FCSTD DOCUMENT  (FreeCAD 0.18R4 (GitTag))
Label: pcb_0721
License: All rights reserved
LicenseURL: http://en.wikipedia.org/wiki/All_rights_reserved
objects: Part::Extrusion×98, Part::Feature×92, Part::Cut×38, Part::Part2DObjectPython×5, Part::MultiFuse×2
note: 235 computed .brp shape members not serialized (recipe doc carries the construction recipe); baked Part::Feature solids carry a one-line shape summary decoded from their .brp

FEATURE [Part::Feature] path847002
  shape: bbox 52.06 x 32.88 x 2e-07 mm, 1 faces, 0 solids (baked)
FEATURE [Part::Feature] path847003
  shape: bbox 1.07 x 1.07 x 2e-07 mm, 1 faces, 0 solids (baked)
FEATURE [Part::Feature] path847004
  shape: bbox 1.07 x 1.07 x 2e-07 mm, 1 faces, 0 solids (baked)
FEATURE [Part::Feature] path847005
  shape: bbox 1.07 x 1.07 x 2e-07 mm, 1 faces, 0 solids (baked)
FEATURE [Part::Feature] path847006
  shape: bbox 3.193 x 3.179 x 2e-07 mm, 1 faces, 0 solids (baked)
FEATURE [Part::Feature] path847007
  shape: bbox 2.86 x 2.857 x 2e-07 mm, 1 faces, 0 solids (baked)
FEATURE [Part::Feature] path847008
  shape: bbox 9.356 x 7.483 x 2e-07 mm, 1 faces, 0 solids (baked)
FEATURE [Part::Feature] path847009
  shape: bbox 0.8865 x 0.8873 x 2e-07 mm, 1 faces, 0 solids (baked)
FEATURE [Part::Feature] path847010
  shape: bbox 3.193 x 3.179 x 2e-07 mm, 1 faces, 0 solids (baked)
FEATURE [Part::Feature] path847011
  shape: bbox 2.86 x 2.857 x 2e-07 mm, 1 faces, 0 solids (baked)
FEATURE [Part::Feature] path847012
  shape: bbox 48.4 x 29.19 x 2e-07 mm, 1 faces, 0 solids (baked)
FEATURE [Part::Feature] path847013
  shape: bbox 0.8865 x 0.8873 x 2e-07 mm, 1 faces, 0 solids (baked)
FEATURE [Part::Feature] path847014
  shape: bbox 1.08 x 1.08 x 2e-07 mm, 1 faces, 0 solids (baked)
FEATURE [Part::Feature] path847015
  shape: bbox 1.051 x 1.08 x 2e-07 mm, 1 faces, 0 solids (baked)
FEATURE [Part::Feature] path847016
  shape: bbox 0.8865 x 0.8873 x 2e-07 mm, 1 faces, 0 solids (baked)
FEATURE [Part::Feature] path847017
  shape: bbox 1.051 x 1.08 x 2e-07 mm, 1 faces, 0 solids (baked)
FEATURE [Part::Feature] path847018
  shape: bbox 1.051 x 1.08 x 2e-07 mm, 1 faces, 0 solids (baked)
FEATURE [Part::Feature] path847019
  shape: bbox 0.8865 x 0.8873 x 2e-07 mm, 1 faces, 0 solids (baked)
FEATURE [Part::Feature] path847020
  shape: bbox 1.07 x 1.07 x 2e-07 mm, 1 faces, 0 solids (baked)
FEATURE [Part::Feature] path847021
  shape: bbox 1.07 x 1.07 x 2e-07 mm, 1 faces, 0 solids (baked)
FEATURE [Part::Feature] path847022
  shape: bbox 1.07 x 1.07 x 2e-07 mm, 1 faces, 0 solids (baked)
FEATURE [Part::Feature] path847023
  shape: bbox 5.68 x 13.71 x 2e-07 mm, 1 faces, 0 solids (baked)
FEATURE [Part::Feature] path847024
  shape: bbox 0.8865 x 0.8873 x 2e-07 mm, 1 faces, 0 solids (baked)
FEATURE [Part::Feature] path847025
  shape: bbox 2.945 x 12.44 x 2e-07 mm, 1 faces, 0 solids (baked)
FEATURE [Part::Feature] path847026
  shape: bbox 1.08 x 1.08 x 2e-07 mm, 1 faces, 0 solids (baked)
FEATURE [Part::Feature] path847027
  shape: bbox 3.892 x 11.64 x 2e-07 mm, 1 faces, 0 solids (baked)
FEATURE [Part::Feature] path847028
  shape: bbox 1.08 x 1.08 x 2e-07 mm, 1 faces, 0 solids (baked)
FEATURE [Part::Feature] path847029
  shape: bbox 3.945 x 10.51 x 2e-07 mm, 1 faces, 0 solids (baked)
FEATURE [Part::Feature] path847030
  shape: bbox 1.08 x 1.08 x 2e-07 mm, 1 faces, 0 solids (baked)
FEATURE [Part::Feature] path847031
  shape: bbox 7.44 x 14.82 x 2e-07 mm, 1 faces, 0 solids (baked)
FEATURE [Part::Feature] path847032
  shape: bbox 1.08 x 1.08 x 2e-07 mm, 1 faces, 0 solids (baked)
FEATURE [Part::Feature] path847033
  shape: bbox 6.314 x 15.06 x 2e-07 mm, 1 faces, 0 solids (baked)
FEATURE [Part::Feature] path847034
  shape: bbox 1.051 x 1.08 x 2e-07 mm, 1 faces, 0 solids (baked)
FEATURE [Part::Feature] path847035
  shape: bbox 1.051 x 1.08 x 2e-07 mm, 1 faces, 0 solids (baked)
FEATURE [Part::Feature] path847036
  shape: bbox 6.567 x 15.06 x 2e-07 mm, 1 faces, 0 solids (baked)
FEATURE [Part::Feature] path847037
  shape: bbox 1.051 x 1.08 x 2e-07 mm, 1 faces, 0 solids (baked)
FEATURE [Part::Feature] path847038
  shape: bbox 1.051 x 1.08 x 2e-07 mm, 1 faces, 0 solids (baked)
FEATURE [Part::Feature] path847039
  shape: bbox 1.051 x 1.08 x 2e-07 mm, 1 faces, 0 solids (baked)
FEATURE [Part::Feature] path847040
  shape: bbox 4.046 x 8.522 x 2e-07 mm, 1 faces, 0 solids (baked)
FEATURE [Part::Feature] path847041
  shape: bbox 1.051 x 1.08 x 2e-07 mm, 1 faces, 0 solids (baked)
FEATURE [Part::Feature] path847042
  shape: bbox 1.051 x 1.08 x 2e-07 mm, 1 faces, 0 solids (baked)
FEATURE [Part::Feature] path847043
  shape: bbox 6.997 x 11.98 x 2e-07 mm, 1 faces, 0 solids (baked)
FEATURE [Part::Feature] path847044
  shape: bbox 4.686 x 5.267 x 2e-07 mm, 1 faces, 0 solids (baked)
FEATURE [Part::Feature] path847045
  shape: bbox 3.177 x 19.4 x 2e-07 mm, 1 faces, 0 solids (baked)
FEATURE [Part::Feature] path847046
  shape: bbox 2.39 x 7.265 x 2e-07 mm, 1 faces, 0 solids (baked)
FEATURE [Part::Feature] path847047
  shape: bbox 3.317 x 3.796 x 2e-07 mm, 1 faces, 0 solids (baked)
FEATURE [Part::Feature] path847048
  shape: bbox 0.8865 x 0.8873 x 2e-07 mm, 1 faces, 0 solids (baked)
FEATURE [Part::Feature] path847049
  shape: bbox 1.509 x 4.212 x 2e-07 mm, 1 faces, 0 solids (baked)
FEATURE [Part::Feature] path847050
  shape: bbox 6.111 x 3.927 x 2e-07 mm, 1 faces, 0 solids (baked)
FEATURE [Part::Feature] path847051 .. path847054  x4 (patterned run collapsed; names and placements below)
  shape: bbox 0.5594 x 1.274 x 2e-07 mm, 1 faces, 0 solids (baked)
FEATURE [Part::Feature] path847055
  shape: bbox 1.277 x 0.5581 x 2e-07 mm, 1 faces, 0 solids (baked)
FEATURE [Part::Feature] path847056
  shape: bbox 1.277 x 0.5581 x 2e-07 mm, 1 faces, 0 solids (baked)
FEATURE [Part::Feature] path847057
  shape: bbox 2.818 x 3.254 x 2e-07 mm, 1 faces, 0 solids (baked)
FEATURE [Part::Feature] path847058
  shape: bbox 0.781 x 0.783 x 2e-07 mm, 1 faces, 0 solids (baked)
FEATURE [Part::Feature] path847059
  shape: bbox 2.206 x 0.6002 x 2e-07 mm, 1 faces, 0 solids (baked)
FEATURE [Part::Feature] path847060
  shape: bbox 1.277 x 0.5581 x 2e-07 mm, 1 faces, 0 solids (baked)
FEATURE [Part::Feature] path847061
  shape: bbox 1.277 x 0.5581 x 2e-07 mm, 1 faces, 0 solids (baked)
FEATURE [Part::Feature] path847062
  shape: bbox 1.277 x 0.5581 x 2e-07 mm, 1 faces, 0 solids (baked)
FEATURE [Part::Feature] path847063
  shape: bbox 3.367 x 1.611 x 2e-07 mm, 1 faces, 0 solids (baked)
FEATURE [Part::Feature] path847064
  shape: bbox 0.781 x 0.783 x 2e-07 mm, 1 faces, 0 solids (baked)
FEATURE [Part::Feature] path847065
  shape: bbox 9.762 x 5.519 x 2e-07 mm, 1 faces, 0 solids (baked)
FEATURE [Part::Feature] path847066
  shape: bbox 2.206 x 0.6002 x 2e-07 mm, 1 faces, 0 solids (baked)
FEATURE [Part::Feature] path847067
  shape: bbox 2.206 x 0.6002 x 2e-07 mm, 1 faces, 0 solids (baked)
FEATURE [Part::Feature] path847068
  shape: bbox 5.456 x 11.92 x 2e-07 mm, 1 faces, 0 solids (baked)
FEATURE [Part::Feature] path847069
  shape: bbox 0.781 x 0.783 x 2e-07 mm, 1 faces, 0 solids (baked)
FEATURE [Part::Feature] path847070
  shape: bbox 0.8865 x 0.8873 x 2e-07 mm, 1 faces, 0 solids (baked)
FEATURE [Part::Feature] path847071
  shape: bbox 4.58 x 1.611 x 2e-07 mm, 1 faces, 0 solids (baked)
FEATURE [Part::Feature] path847072
  shape: bbox 0.781 x 0.783 x 2e-07 mm, 1 faces, 0 solids (baked)
FEATURE [Part::Feature] path847073
  shape: bbox 1.277 x 0.5581 x 2e-07 mm, 1 faces, 0 solids (baked)
FEATURE [Part::Feature] path847074
  shape: bbox 18.21 x 6.191 x 2e-07 mm, 1 faces, 0 solids (baked)
FEATURE [Part::Feature] path847075
  shape: bbox 12.52 x 5.875 x 2e-07 mm, 1 faces, 0 solids (baked)
FEATURE [Part::Feature] path847076
  shape: bbox 3.887 x 4.512 x 2e-07 mm, 1 faces, 0 solids (baked)
FEATURE [Part::Feature] path847077
  shape: bbox 0.781 x 0.783 x 2e-07 mm, 1 faces, 0 solids (baked)
FEATURE [Part::Feature] path847078
  shape: bbox 0.8865 x 0.8873 x 2e-07 mm, 1 faces, 0 solids (baked)
FEATURE [Part::Feature] path847079
  shape: bbox 3.261 x 1.611 x 2e-07 mm, 1 faces, 0 solids (baked)
FEATURE [Part::Feature] path847080
  shape: bbox 0.781 x 0.783 x 2e-07 mm, 1 faces, 0 solids (baked)
FEATURE [Part::Feature] path847081
  shape: bbox 15.05 x 6.086 x 2e-07 mm, 1 faces, 0 solids (baked)
FEATURE [Part::Feature] path847082
  shape: bbox 9.667 x 8.824 x 2e-07 mm, 1 faces, 0 solids (baked)
FEATURE [Part::Feature] path847083
  shape: bbox 7.852 x 8.824 x 2e-07 mm, 1 faces, 0 solids (baked)
FEATURE [Part::Feature] path847084
  shape: bbox 0.5594 x 1.274 x 2e-07 mm, 1 faces, 0 solids (baked)
FEATURE [Part::Feature] path847085
  shape: bbox 0.5594 x 1.274 x 2e-07 mm, 1 faces, 0 solids (baked)
FEATURE [Part::Feature] path847086
  shape: bbox 7.129 x 2.592 x 2e-07 mm, 1 faces, 0 solids (baked)
FEATURE [Part::Feature] path847087
  shape: bbox 0.8865 x 0.8873 x 2e-07 mm, 1 faces, 0 solids (baked)
FEATURE [Part::Feature] path847088
  shape: bbox 7.129 x 3.676 x 2e-07 mm, 1 faces, 0 solids (baked)
FEATURE [Part::Feature] path847089
  shape: bbox 0.8865 x 0.8873 x 2e-07 mm, 1 faces, 0 solids (baked)
FEATURE [Part::Feature] path847090
  shape: bbox 3.193 x 3.187 x 2e-07 mm, 1 faces, 0 solids (baked)
FEATURE [Part::Feature] path847091
  shape: bbox 2.86 x 2.857 x 2e-07 mm, 1 faces, 0 solids (baked)
FEATURE [Part::Feature] path847092
  shape: bbox 3.193 x 3.187 x 2e-07 mm, 1 faces, 0 solids (baked)
FEATURE [Part::Feature] path847093
  shape: bbox 2.86 x 2.857 x 2e-07 mm, 1 faces, 0 solids (baked)
FEATURE [Part::Extrusion] Extrude
  Base = -> path847002
  Dir = (0,0,1)
  DirMode = 0
  FaceMakerClass = Part::FaceMakerBullseye
  LengthFwd = 10
  LengthRev = 0
  Solid = false
  Symmetric = false
FEATURE [Part::Extrusion] Extrude001
  Base = -> path847003
  Dir = (0,0,1)
  DirMode = 0
  FaceMakerClass = Part::FaceMakerBullseye
  LengthFwd = 10
  LengthRev = 0
  Solid = false
  Symmetric = false
FEATURE [Part::Extrusion] Extrude002
  Base = -> path847004
  Dir = (0,0,1)
  DirMode = 0
  FaceMakerClass = Part::FaceMakerBullseye
  LengthFwd = 10
  LengthRev = 0
  Solid = false
  Symmetric = false
FEATURE [Part::Extrusion] Extrude003
  Base = -> path847005
  Dir = (0,0,1)
  DirMode = 0
  FaceMakerClass = Part::FaceMakerBullseye
  LengthFwd = 10
  LengthRev = 0
  Solid = false
  Symmetric = false
FEATURE [Part::Extrusion] Extrude004
  Base = -> path847006
  Dir = (0,0,1)
  DirMode = 0
  FaceMakerClass = Part::FaceMakerBullseye
  LengthFwd = 10
  LengthRev = 0
  Solid = false
  Symmetric = false
FEATURE [Part::Extrusion] Extrude005
  Base = -> path847007
  Dir = (0,0,1)
  DirMode = 0
  FaceMakerClass = Part::FaceMakerBullseye
  LengthFwd = 10
  LengthRev = 0
  Solid = false
  Symmetric = false
FEATURE [Part::Extrusion] Extrude006
  Base = -> path847008
  Dir = (0,0,1)
  DirMode = 0
  FaceMakerClass = Part::FaceMakerBullseye
  LengthFwd = 10
  LengthRev = 0
  Solid = false
  Symmetric = false
FEATURE [Part::Extrusion] Extrude007
  Base = -> path847009
  Dir = (0,0,1)
  DirMode = 0
  FaceMakerClass = Part::FaceMakerBullseye
  LengthFwd = 10
  LengthRev = 0
  Solid = false
  Symmetric = false
FEATURE [Part::Extrusion] Extrude008
  Base = -> path847010
  Dir = (0,0,1)
  DirMode = 0
  FaceMakerClass = Part::FaceMakerBullseye
  LengthFwd = 10
  LengthRev = 0
  Solid = false
  Symmetric = false
FEATURE [Part::Extrusion] Extrude009
  Base = -> path847011
  Dir = (0,0,1)
  DirMode = 0
  FaceMakerClass = Part::FaceMakerBullseye
  LengthFwd = 10
  LengthRev = 0
  Solid = false
  Symmetric = false
FEATURE [Part::Extrusion] Extrude010
  Base = -> path847012
  Dir = (0,0,1)
  DirMode = 0
  FaceMakerClass = Part::FaceMakerBullseye
  LengthFwd = 10
  LengthRev = 0
  Solid = false
  Symmetric = false
FEATURE [Part::Extrusion] Extrude011
  Base = -> path847013
  Dir = (0,0,1)
  DirMode = 0
  FaceMakerClass = Part::FaceMakerBullseye
  LengthFwd = 10
  LengthRev = 0
  Solid = false
  Symmetric = false
FEATURE [Part::Extrusion] Extrude012
  Base = -> path847014
  Dir = (0,0,1)
  DirMode = 0
  FaceMakerClass = Part::FaceMakerBullseye
  LengthFwd = 10
  LengthRev = 0
  Solid = false
  Symmetric = false
FEATURE [Part::Extrusion] Extrude013
  Base = -> path847015
  Dir = (0,0,1)
  DirMode = 0
  FaceMakerClass = Part::FaceMakerBullseye
  LengthFwd = 10
  LengthRev = 0
  Solid = false
  Symmetric = false
FEATURE [Part::Extrusion] Extrude014
  Base = -> path847016
  Dir = (0,0,1)
  DirMode = 0
  FaceMakerClass = Part::FaceMakerBullseye
  LengthFwd = 10
  LengthRev = 0
  Solid = false
  Symmetric = false
FEATURE [Part::Extrusion] Extrude015
  Base = -> path847017
  Dir = (0,0,1)
  DirMode = 0
  FaceMakerClass = Part::FaceMakerBullseye
  LengthFwd = 10
  LengthRev = 0
  Solid = false
  Symmetric = false
FEATURE [Part::Extrusion] Extrude016
  Base = -> path847018
  Dir = (0,0,1)
  DirMode = 0
  FaceMakerClass = Part::FaceMakerBullseye
  LengthFwd = 10
  LengthRev = 0
  Solid = false
  Symmetric = false
FEATURE [Part::Extrusion] Extrude017
  Base = -> path847019
  Dir = (0,0,1)
  DirMode = 0
  FaceMakerClass = Part::FaceMakerBullseye
  LengthFwd = 10
  LengthRev = 0
  Solid = false
  Symmetric = false
FEATURE [Part::Extrusion] Extrude018
  Base = -> path847020
  Dir = (0,0,1)
  DirMode = 0
  FaceMakerClass = Part::FaceMakerBullseye
  LengthFwd = 10
  LengthRev = 0
  Solid = false
  Symmetric = false
FEATURE [Part::Extrusion] Extrude019
  Base = -> path847021
  Dir = (0,0,1)
  DirMode = 0
  FaceMakerClass = Part::FaceMakerBullseye
  LengthFwd = 10
  LengthRev = 0
  Solid = false
  Symmetric = false
FEATURE [Part::Extrusion] Extrude020
  Base = -> path847022
  Dir = (0,0,1)
  DirMode = 0
  FaceMakerClass = Part::FaceMakerBullseye
  LengthFwd = 10
  LengthRev = 0
  Solid = false
  Symmetric = false
FEATURE [Part::Extrusion] Extrude021
  Base = -> path847023
  Dir = (0,0,1)
  DirMode = 0
  FaceMakerClass = Part::FaceMakerBullseye
  LengthFwd = 10
  LengthRev = 0
  Solid = false
  Symmetric = false
FEATURE [Part::Extrusion] Extrude022
  Base = -> path847024
  Dir = (0,0,1)
  DirMode = 0
  FaceMakerClass = Part::FaceMakerBullseye
  LengthFwd = 10
  LengthRev = 0
  Solid = false
  Symmetric = false
FEATURE [Part::Extrusion] Extrude023
  Base = -> path847025
  Dir = (0,0,1)
  DirMode = 0
  FaceMakerClass = Part::FaceMakerBullseye
  LengthFwd = 10
  LengthRev = 0
  Solid = false
  Symmetric = false
FEATURE [Part::Extrusion] Extrude024
  Base = -> path847026
  Dir = (0,0,1)
  DirMode = 0
  FaceMakerClass = Part::FaceMakerBullseye
  LengthFwd = 10
  LengthRev = 0
  Solid = false
  Symmetric = false
FEATURE [Part::Extrusion] Extrude025
  Base = -> path847027
  Dir = (0,0,1)
  DirMode = 0
  FaceMakerClass = Part::FaceMakerBullseye
  LengthFwd = 10
  LengthRev = 0
  Solid = false
  Symmetric = false
FEATURE [Part::Extrusion] Extrude026
  Base = -> path847028
  Dir = (0,0,1)
  DirMode = 0
  FaceMakerClass = Part::FaceMakerBullseye
  LengthFwd = 10
  LengthRev = 0
  Solid = false
  Symmetric = false
FEATURE [Part::Extrusion] Extrude027
  Base = -> path847029
  Dir = (0,0,1)
  DirMode = 0
  FaceMakerClass = Part::FaceMakerBullseye
  LengthFwd = 10
  LengthRev = 0
  Solid = false
  Symmetric = false
FEATURE [Part::Extrusion] Extrude028
  Base = -> path847030
  Dir = (0,0,1)
  DirMode = 0
  FaceMakerClass = Part::FaceMakerBullseye
  LengthFwd = 10
  LengthRev = 0
  Solid = false
  Symmetric = false
FEATURE [Part::Extrusion] Extrude029
  Base = -> path847031
  Dir = (0,0,1)
  DirMode = 0
  FaceMakerClass = Part::FaceMakerBullseye
  LengthFwd = 10
  LengthRev = 0
  Solid = false
  Symmetric = false
FEATURE [Part::Extrusion] Extrude030
  Base = -> path847032
  Dir = (0,0,1)
  DirMode = 0
  FaceMakerClass = Part::FaceMakerBullseye
  LengthFwd = 10
  LengthRev = 0
  Solid = false
  Symmetric = false
FEATURE [Part::Extrusion] Extrude031
  Base = -> path847033
  Dir = (0,0,1)
  DirMode = 0
  FaceMakerClass = Part::FaceMakerBullseye
  LengthFwd = 10
  LengthRev = 0
  Solid = false
  Symmetric = false
FEATURE [Part::Extrusion] Extrude032
  Base = -> path847034
  Dir = (0,0,1)
  DirMode = 0
  FaceMakerClass = Part::FaceMakerBullseye
  LengthFwd = 10
  LengthRev = 0
  Solid = false
  Symmetric = false
FEATURE [Part::Extrusion] Extrude033
  Base = -> path847035
  Dir = (0,0,1)
  DirMode = 0
  FaceMakerClass = Part::FaceMakerBullseye
  LengthFwd = 10
  LengthRev = 0
  Solid = false
  Symmetric = false
FEATURE [Part::Extrusion] Extrude034
  Base = -> path847036
  Dir = (0,0,1)
  DirMode = 0
  FaceMakerClass = Part::FaceMakerBullseye
  LengthFwd = 10
  LengthRev = 0
  Solid = false
  Symmetric = false
FEATURE [Part::Extrusion] Extrude035
  Base = -> path847037
  Dir = (0,0,1)
  DirMode = 0
  FaceMakerClass = Part::FaceMakerBullseye
  LengthFwd = 10
  LengthRev = 0
  Solid = false
  Symmetric = false
FEATURE [Part::Extrusion] Extrude036
  Base = -> path847038
  Dir = (0,0,1)
  DirMode = 0
  FaceMakerClass = Part::FaceMakerBullseye
  LengthFwd = 10
  LengthRev = 0
  Solid = false
  Symmetric = false
FEATURE [Part::Extrusion] Extrude037
  Base = -> path847039
  Dir = (0,0,1)
  DirMode = 0
  FaceMakerClass = Part::FaceMakerBullseye
  LengthFwd = 10
  LengthRev = 0
  Solid = false
  Symmetric = false
FEATURE [Part::Extrusion] Extrude038
  Base = -> path847040
  Dir = (0,0,1)
  DirMode = 0
  FaceMakerClass = Part::FaceMakerBullseye
  LengthFwd = 10
  LengthRev = 0
  Solid = false
  Symmetric = false
FEATURE [Part::Extrusion] Extrude039
  Base = -> path847041
  Dir = (0,0,1)
  DirMode = 0
  FaceMakerClass = Part::FaceMakerBullseye
  LengthFwd = 10
  LengthRev = 0
  Solid = false
  Symmetric = false
FEATURE [Part::Extrusion] Extrude040
  Base = -> path847042
  Dir = (0,0,1)
  DirMode = 0
  FaceMakerClass = Part::FaceMakerBullseye
  LengthFwd = 10
  LengthRev = 0
  Solid = false
  Symmetric = false
FEATURE [Part::Extrusion] Extrude041
  Base = -> path847043
  Dir = (0,0,1)
  DirMode = 0
  FaceMakerClass = Part::FaceMakerBullseye
  LengthFwd = 10
  LengthRev = 0
  Solid = false
  Symmetric = false
FEATURE [Part::Extrusion] Extrude042
  Base = -> path847044
  Dir = (0,0,1)
  DirMode = 0
  FaceMakerClass = Part::FaceMakerBullseye
  LengthFwd = 10
  LengthRev = 0
  Solid = false
  Symmetric = false
FEATURE [Part::Extrusion] Extrude043
  Base = -> path847045
  Dir = (0,0,1)
  DirMode = 0
  FaceMakerClass = Part::FaceMakerBullseye
  LengthFwd = 10
  LengthRev = 0
  Solid = false
  Symmetric = false
FEATURE [Part::Extrusion] Extrude044
  Base = -> path847046
  Dir = (0,0,1)
  DirMode = 0
  FaceMakerClass = Part::FaceMakerBullseye
  LengthFwd = 10
  LengthRev = 0
  Solid = false
  Symmetric = false
FEATURE [Part::Extrusion] Extrude045
  Base = -> path847047
  Dir = (0,0,1)
  DirMode = 0
  FaceMakerClass = Part::FaceMakerBullseye
  LengthFwd = 10
  LengthRev = 0
  Solid = false
  Symmetric = false
FEATURE [Part::Extrusion] Extrude046
  Base = -> path847048
  Dir = (0,0,1)
  DirMode = 0
  FaceMakerClass = Part::FaceMakerBullseye
  LengthFwd = 10
  LengthRev = 0
  Solid = false
  Symmetric = false
FEATURE [Part::Extrusion] Extrude047
  Base = -> path847049
  Dir = (0,0,1)
  DirMode = 0
  FaceMakerClass = Part::FaceMakerBullseye
  LengthFwd = 10
  LengthRev = 0
  Solid = false
  Symmetric = false
FEATURE [Part::Extrusion] Extrude048
  Base = -> path847050
  Dir = (0,0,1)
  DirMode = 0
  FaceMakerClass = Part::FaceMakerBullseye
  LengthFwd = 10
  LengthRev = 0
  Solid = false
  Symmetric = false
FEATURE [Part::Extrusion] Extrude049
  Base = -> path847051
  Dir = (0,0,1)
  DirMode = 0
  FaceMakerClass = Part::FaceMakerBullseye
  LengthFwd = 10
  LengthRev = 0
  Solid = false
  Symmetric = false
FEATURE [Part::Extrusion] Extrude050
  Base = -> path847052
  Dir = (0,0,1)
  DirMode = 0
  FaceMakerClass = Part::FaceMakerBullseye
  LengthFwd = 10
  LengthRev = 0
  Solid = false
  Symmetric = false
FEATURE [Part::Extrusion] Extrude051
  Base = -> path847053
  Dir = (0,0,1)
  DirMode = 0
  FaceMakerClass = Part::FaceMakerBullseye
  LengthFwd = 10
  LengthRev = 0
  Solid = false
  Symmetric = false
FEATURE [Part::Extrusion] Extrude052
  Base = -> path847054
  Dir = (0,0,1)
  DirMode = 0
  FaceMakerClass = Part::FaceMakerBullseye
  LengthFwd = 10
  LengthRev = 0
  Solid = false
  Symmetric = false
FEATURE [Part::Extrusion] Extrude053
  Base = -> path847055
  Dir = (0,0,1)
  DirMode = 0
  FaceMakerClass = Part::FaceMakerBullseye
  LengthFwd = 10
  LengthRev = 0
  Solid = false
  Symmetric = false
FEATURE [Part::Extrusion] Extrude054
  Base = -> path847056
  Dir = (0,0,1)
  DirMode = 0
  FaceMakerClass = Part::FaceMakerBullseye
  LengthFwd = 10
  LengthRev = 0
  Solid = false
  Symmetric = false
FEATURE [Part::Extrusion] Extrude055
  Base = -> path847057
  Dir = (0,0,1)
  DirMode = 0
  FaceMakerClass = Part::FaceMakerBullseye
  LengthFwd = 10
  LengthRev = 0
  Solid = false
  Symmetric = false
FEATURE [Part::Extrusion] Extrude056
  Base = -> path847058
  Dir = (0,0,1)
  DirMode = 0
  FaceMakerClass = Part::FaceMakerBullseye
  LengthFwd = 10
  LengthRev = 0
  Solid = false
  Symmetric = false
FEATURE [Part::Extrusion] Extrude057
  Base = -> path847059
  Dir = (0,0,1)
  DirMode = 0
  FaceMakerClass = Part::FaceMakerBullseye
  LengthFwd = 10
  LengthRev = 0
  Solid = false
  Symmetric = false
FEATURE [Part::Extrusion] Extrude058
  Base = -> path847060
  Dir = (0,0,1)
  DirMode = 0
  FaceMakerClass = Part::FaceMakerBullseye
  LengthFwd = 10
  LengthRev = 0
  Solid = false
  Symmetric = false
FEATURE [Part::Extrusion] Extrude059
  Base = -> path847061
  Dir = (0,0,1)
  DirMode = 0
  FaceMakerClass = Part::FaceMakerBullseye
  LengthFwd = 10
  LengthRev = 0
  Solid = false
  Symmetric = false
FEATURE [Part::Extrusion] Extrude060
  Base = -> path847062
  Dir = (0,0,1)
  DirMode = 0
  FaceMakerClass = Part::FaceMakerBullseye
  LengthFwd = 10
  LengthRev = 0
  Solid = false
  Symmetric = false
FEATURE [Part::Extrusion] Extrude061
  Base = -> path847063
  Dir = (0,0,1)
  DirMode = 0
  FaceMakerClass = Part::FaceMakerBullseye
  LengthFwd = 10
  LengthRev = 0
  Solid = false
  Symmetric = false
FEATURE [Part::Extrusion] Extrude062
  Base = -> path847064
  Dir = (0,0,1)
  DirMode = 0
  FaceMakerClass = Part::FaceMakerBullseye
  LengthFwd = 10
  LengthRev = 0
  Solid = false
  Symmetric = false
FEATURE [Part::Extrusion] Extrude063
  Base = -> path847065
  Dir = (0,0,1)
  DirMode = 0
  FaceMakerClass = Part::FaceMakerBullseye
  LengthFwd = 10
  LengthRev = 0
  Solid = false
  Symmetric = false
FEATURE [Part::Extrusion] Extrude064
  Base = -> path847066
  Dir = (0,0,1)
  DirMode = 0
  FaceMakerClass = Part::FaceMakerBullseye
  LengthFwd = 10
  LengthRev = 0
  Solid = false
  Symmetric = false
FEATURE [Part::Extrusion] Extrude065
  Base = -> path847067
  Dir = (0,0,1)
  DirMode = 0
  FaceMakerClass = Part::FaceMakerBullseye
  LengthFwd = 10
  LengthRev = 0
  Solid = false
  Symmetric = false
FEATURE [Part::Extrusion] Extrude066
  Base = -> path847068
  Dir = (0,0,1)
  DirMode = 0
  FaceMakerClass = Part::FaceMakerBullseye
  LengthFwd = 10
  LengthRev = 0
  Solid = false
  Symmetric = false
FEATURE [Part::Extrusion] Extrude067
  Base = -> path847069
  Dir = (0,0,1)
  DirMode = 0
  FaceMakerClass = Part::FaceMakerBullseye
  LengthFwd = 10
  LengthRev = 0
  Solid = false
  Symmetric = false
FEATURE [Part::Extrusion] Extrude068
  Base = -> path847070
  Dir = (0,0,1)
  DirMode = 0
  FaceMakerClass = Part::FaceMakerBullseye
  LengthFwd = 10
  LengthRev = 0
  Solid = false
  Symmetric = false
FEATURE [Part::Extrusion] Extrude069
  Base = -> path847071
  Dir = (0,0,1)
  DirMode = 0
  FaceMakerClass = Part::FaceMakerBullseye
  LengthFwd = 10
  LengthRev = 0
  Solid = false
  Symmetric = false
FEATURE [Part::Extrusion] Extrude070
  Base = -> path847072
  Dir = (0,0,1)
  DirMode = 0
  FaceMakerClass = Part::FaceMakerBullseye
  LengthFwd = 10
  LengthRev = 0
  Solid = false
  Symmetric = false
FEATURE [Part::Extrusion] Extrude071
  Base = -> path847073
  Dir = (0,0,1)
  DirMode = 0
  FaceMakerClass = Part::FaceMakerBullseye
  LengthFwd = 10
  LengthRev = 0
  Solid = false
  Symmetric = false
FEATURE [Part::Extrusion] Extrude072
  Base = -> path847074
  Dir = (0,0,1)
  DirMode = 0
  FaceMakerClass = Part::FaceMakerBullseye
  LengthFwd = 10
  LengthRev = 0
  Solid = false
  Symmetric = false
FEATURE [Part::Extrusion] Extrude073
  Base = -> path847075
  Dir = (0,0,1)
  DirMode = 0
  FaceMakerClass = Part::FaceMakerBullseye
  LengthFwd = 10
  LengthRev = 0
  Solid = false
  Symmetric = false
FEATURE [Part::Extrusion] Extrude074
  Base = -> path847076
  Dir = (0,0,1)
  DirMode = 0
  FaceMakerClass = Part::FaceMakerBullseye
  LengthFwd = 10
  LengthRev = 0
  Solid = false
  Symmetric = false
FEATURE [Part::Extrusion] Extrude075
  Base = -> path847077
  Dir = (0,0,1)
  DirMode = 0
  FaceMakerClass = Part::FaceMakerBullseye
  LengthFwd = 10
  LengthRev = 0
  Solid = false
  Symmetric = false
FEATURE [Part::Extrusion] Extrude076
  Base = -> path847078
  Dir = (0,0,1)
  DirMode = 0
  FaceMakerClass = Part::FaceMakerBullseye
  LengthFwd = 10
  LengthRev = 0
  Solid = false
  Symmetric = false
FEATURE [Part::Extrusion] Extrude077
  Base = -> path847079
  Dir = (0,0,1)
  DirMode = 0
  FaceMakerClass = Part::FaceMakerBullseye
  LengthFwd = 10
  LengthRev = 0
  Solid = false
  Symmetric = false
FEATURE [Part::Extrusion] Extrude078
  Base = -> path847080
  Dir = (0,0,1)
  DirMode = 0
  FaceMakerClass = Part::FaceMakerBullseye
  LengthFwd = 10
  LengthRev = 0
  Solid = false
  Symmetric = false
FEATURE [Part::Extrusion] Extrude079
  Base = -> path847081
  Dir = (0,0,1)
  DirMode = 0
  FaceMakerClass = Part::FaceMakerBullseye
  LengthFwd = 10
  LengthRev = 0
  Solid = false
  Symmetric = false
FEATURE [Part::Extrusion] Extrude080
  Base = -> path847082
  Dir = (0,0,1)
  DirMode = 0
  FaceMakerClass = Part::FaceMakerBullseye
  LengthFwd = 10
  LengthRev = 0
  Solid = false
  Symmetric = false
FEATURE [Part::Extrusion] Extrude081
  Base = -> path847083
  Dir = (0,0,1)
  DirMode = 0
  FaceMakerClass = Part::FaceMakerBullseye
  LengthFwd = 10
  LengthRev = 0
  Solid = false
  Symmetric = false
FEATURE [Part::Extrusion] Extrude082
  Base = -> path847084
  Dir = (0,0,1)
  DirMode = 0
  FaceMakerClass = Part::FaceMakerBullseye
  LengthFwd = 10
  LengthRev = 0
  Solid = false
  Symmetric = false
FEATURE [Part::Extrusion] Extrude083
  Base = -> path847085
  Dir = (0,0,1)
  DirMode = 0
  FaceMakerClass = Part::FaceMakerBullseye
  LengthFwd = 10
  LengthRev = 0
  Solid = false
  Symmetric = false
FEATURE [Part::Extrusion] Extrude084
  Base = -> path847086
  Dir = (0,0,1)
  DirMode = 0
  FaceMakerClass = Part::FaceMakerBullseye
  LengthFwd = 10
  LengthRev = 0
  Solid = false
  Symmetric = false
FEATURE [Part::Extrusion] Extrude085
  Base = -> path847087
  Dir = (0,0,1)
  DirMode = 0
  FaceMakerClass = Part::FaceMakerBullseye
  LengthFwd = 10
  LengthRev = 0
  Solid = false
  Symmetric = false
FEATURE [Part::Extrusion] Extrude086
  Base = -> path847088
  Dir = (0,0,1)
  DirMode = 0
  FaceMakerClass = Part::FaceMakerBullseye
  LengthFwd = 10
  LengthRev = 0
  Solid = false
  Symmetric = false
FEATURE [Part::Extrusion] Extrude087
  Base = -> path847089
  Dir = (0,0,1)
  DirMode = 0
  FaceMakerClass = Part::FaceMakerBullseye
  LengthFwd = 10
  LengthRev = 0
  Solid = false
  Symmetric = false
FEATURE [Part::Extrusion] Extrude088
  Base = -> path847090
  Dir = (0,0,1)
  DirMode = 0
  FaceMakerClass = Part::FaceMakerBullseye
  LengthFwd = 10
  LengthRev = 0
  Solid = false
  Symmetric = false
FEATURE [Part::Extrusion] Extrude089
  Base = -> path847091
  Dir = (0,0,1)
  DirMode = 0
  FaceMakerClass = Part::FaceMakerBullseye
  LengthFwd = 10
  LengthRev = 0
  Solid = false
  Symmetric = false
FEATURE [Part::Extrusion] Extrude090
  Base = -> path847092
  Dir = (0,0,1)
  DirMode = 0
  FaceMakerClass = Part::FaceMakerBullseye
  LengthFwd = 10
  LengthRev = 0
  Solid = false
  Symmetric = false
FEATURE [Part::Extrusion] Extrude091
  Base = -> path847093
  Dir = (0,0,1)
  DirMode = 0
  FaceMakerClass = Part::FaceMakerBullseye
  LengthFwd = 10
  LengthRev = 0
  Solid = false
  Symmetric = false
FEATURE [Part::Cut] Cut
  Base = -> Extrude061
  Tool = -> Extrude062
FEATURE [Part::Cut] Cut001
  Base = -> Extrude069
  Tool = -> Extrude070
FEATURE [Part::Cut] Cut002
  Base = -> Extrude077
  Tool = -> Extrude078
FEATURE [Part::Cut] Cut003
  Base = -> Extrude074
  Tool = -> Extrude076
FEATURE [Part::Cut] Cut004
  Base = -> Cut003
  Tool = -> Extrude075
FEATURE [Part::Cut] Cut005
  Base = -> Extrude084
  Tool = -> Extrude085
FEATURE [Part::Cut] Cut006
  Base = -> Extrude066
  Tool = -> Extrude067
FEATURE [Part::Cut] Cut007
  Base = -> Extrude055
  Tool = -> Extrude056
FEATURE [Part::Cut] Cut008
  Base = -> Cut006
  Tool = -> Extrude068
FEATURE [Part::Cut] Cut009
  Base = -> Extrude086
  Tool = -> Extrude087
FEATURE [Part::Cut] Cut010
  Base = -> Extrude045
  Tool = -> Extrude046
FEATURE [Part::Cut] Cut011
  Base = -> Extrude010
  Tool = -> Extrude017
FEATURE [Part::Cut] Cut012
  Base = -> Cut011
  Tool = -> Extrude014
FEATURE [Part::Cut] Cut013
  Base = -> Cut012
  Tool = -> Extrude011
FEATURE [Part::Cut] Cut014
  Base = -> Extrude006
  Tool = -> Extrude007
FEATURE [Part::Cut] Cut015
  Base = -> Cut013
  Tool = -> Extrude018
FEATURE [Part::Cut] Cut016
  Base = -> Cut015
  Tool = -> Extrude019
FEATURE [Part::Cut] Cut017
  Base = -> Cut016
  Tool = -> Extrude020
FEATURE [Part::Cut] Cut018
  Base = -> Extrude
  Tool = -> Extrude001
FEATURE [Part::Cut] Cut019
  Base = -> Cut018
  Tool = -> Extrude002
FEATURE [Part::Cut] Cut020
  Base = -> Cut019
  Tool = -> Extrude003
FEATURE [Part::Cut] Cut021
  Base = -> Extrude023
  Tool = -> Extrude024
FEATURE [Part::Cut] Cut022
  Base = -> Extrude025
  Tool = -> Extrude026
FEATURE [Part::Cut] Cut023
  Base = -> Extrude027
  Tool = -> Extrude028
FEATURE [Part::Cut] Cut024
  Base = -> Cut017
  Tool = -> Extrude012
FEATURE [Part::Cut] Cut025
  Base = -> Extrude029
  Tool = -> Extrude030
FEATURE [Part::Cut] Cut026
  Base = -> Cut024
  Tool = -> Extrude015
FEATURE [Part::Cut] Cut027
  Base = -> Cut026
  Tool = -> Extrude016
FEATURE [Part::Cut] Cut028
  Base = -> Cut027
  Tool = -> Extrude013
FEATURE [Part::Cut] Cut029
  Base = -> Extrude034
  Tool = -> Extrude035
FEATURE [Part::Cut] Cut030
  Base = -> Cut029
  Tool = -> Extrude036
FEATURE [Part::Cut] Cut031
  Base = -> Cut030
  Tool = -> Extrude037
FEATURE [Part::Cut] Cut032
  Base = -> Extrude038
  Tool = -> Extrude040
FEATURE [Part::Cut] Cut033
  Base = -> Cut032
  Tool = -> Extrude039
FEATURE [Part::Cut] Cut034
  Base = -> Extrude031
  Tool = -> Extrude032
FEATURE [Part::Cut] Cut035
  Base = -> Cut034
  Tool = -> Extrude033
FEATURE [Part::Cut] Cut036
  Base = -> Extrude021
  Tool = -> Extrude022
FEATURE [Part::MultiFuse] Fusion
  Shapes = -> [Cut036,Cut005,Cut023,Extrude053,Extrude005,Extrude004,Extrude008,Extrude009,Extrude049,Extrude050,Extrude051,Extrude044,Extrude052,Extrude042,Extrude043,Extrude047,Extrude041,Extrude048,Extrude060,Extrude072,Extrude065,Extrude054,Extrude059,Extrude079,Extrude090,Extrude091,Extrude058,Extrude057,Extrude071,Extrude063,Extrude064,Extrude073,Extrude080,Extrude082,Extrude081,Extrude083,Extrude088,+18 more]
FEATURE [Part::Part2DObjectPython] Rectangle  # Draft 2D object (typed FeaturePython)
  ChamferSize = 0
  Columns = 1
  FilletRadius = 0
  Height = 34.8315
  Length = 64.6627
  MakeFace = false
  Placement = pos=(67.8363,-67.2127,0) rot=(0,0,1;0rad)
  Rows = 1
FEATURE [Part::Extrusion] Extrude092
  Base = -> Rectangle
  Dir = (0,0,1)
  DirMode = 0
  FaceMakerClass = Part::FaceMakerBullseye
  LengthFwd = 10
  LengthRev = 0
  Solid = true
  Symmetric = false
FEATURE [Part::Cut] Cut037
  Base = -> Extrude092
  Tool = -> Fusion
FEATURE [Part::Part2DObjectPython] Circle  # Draft 2D object (typed FeaturePython)
  FirstAngle = 0
  LastAngle = 0
  MakeFace = false
  Placement = pos=(130.059,-35.5556,0) rot=(0,0,1;0rad)
  Radius = 0.5
FEATURE [Part::Part2DObjectPython] Circle001  # Draft 2D object (typed FeaturePython)
  FirstAngle = 0
  LastAngle = 0
  MakeFace = false
  Placement = pos=(130.06,-64.7857,0) rot=(0,0,1;0rad)
  Radius = 0.5
FEATURE [Part::Part2DObjectPython] Circle002  # Draft 2D object (typed FeaturePython)
  FirstAngle = 0
  LastAngle = 0
  MakeFace = false
  Placement = pos=(70.7984,-64.7696,0) rot=(0,0,1;0rad)
  Radius = 0.5
FEATURE [Part::Part2DObjectPython] Circle003  # Draft 2D object (typed FeaturePython)
  FirstAngle = 0
  LastAngle = 0
  MakeFace = false
  Placement = pos=(70.7901,-35.8008,0) rot=(0,0,1;0rad)
  Radius = 0.5
FEATURE [Part::Extrusion] Extrude093
  Base = -> Circle
  Dir = (0,0,1)
  DirMode = 0
  FaceMakerClass = Part::FaceMakerBullseye
  LengthFwd = 10
  LengthRev = 0
  Solid = true
  Symmetric = false
FEATURE [Part::Extrusion] Extrude094
  Base = -> Circle001
  Dir = (0,0,1)
  DirMode = 0
  FaceMakerClass = Part::FaceMakerBullseye
  LengthFwd = 10
  LengthRev = 0
  Solid = true
  Symmetric = false
FEATURE [Part::Extrusion] Extrude095
  Base = -> Circle002
  Dir = (0,0,1)
  DirMode = 0
  FaceMakerClass = Part::FaceMakerBullseye
  LengthFwd = 10
  LengthRev = 0
  Solid = true
  Symmetric = false
FEATURE [Part::Extrusion] Extrude096
  Base = -> Circle003
  Dir = (0,0,1)
  DirMode = 0
  FaceMakerClass = Part::FaceMakerBullseye
  LengthFwd = 10
  LengthRev = 0
  Solid = true
  Symmetric = false
FEATURE [Part::Extrusion] Extrude097
  Base = -> Rectangle
  Dir = (0,0,1)
  DirMode = 0
  FaceMakerClass = Part::FaceMakerBullseye
  LengthFwd = 10
  LengthRev = 0
  Solid = true
  Symmetric = false
FEATURE [Part::MultiFuse] Fusion001
  Shapes = -> [Extrude093,Extrude094,Extrude095,Extrude096,Extrude097]
